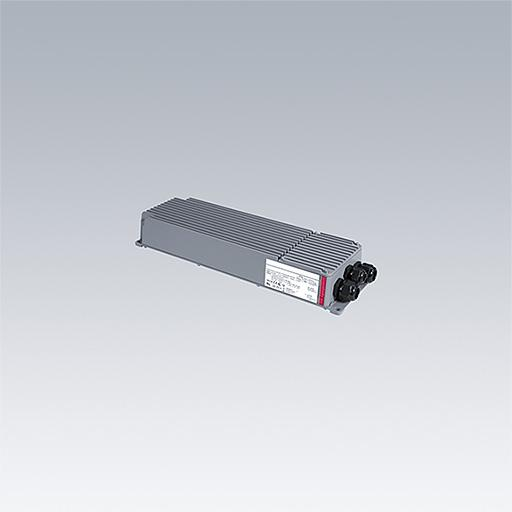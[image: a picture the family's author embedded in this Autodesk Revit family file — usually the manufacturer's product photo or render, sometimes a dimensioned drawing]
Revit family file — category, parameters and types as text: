
# Revit family: Thorn ALTIS GEN5 Gearbox-4 channel gearbox for RGBW
name_source: partatom
category: Electrical Fixtures
units: mm (PartAtom-declared; Revit-internal decimal feet)

## family parameters
Cut with Voids When Loaded = Yes
Host = Face
Maintain Annotation Orientation = No
Part Type = Normal
Room Calculation Point = Yes
Round Connector Dimension = Use Diameter
Shared = Yes

## types (1)
- ALG5 GB 1200W 0.85A 450V 4CH RGBW DMX/DA
    Apparent Load = 1200 VA
    Assembly Code = Pr_60_70_48_54
    Default Elevation = 0 mm  [stored 0 ft]
    Description = LED Control Gear
    Export Type to IFC As = IfcLightFixtureType
    Lamp = LED
    Luminaire Height = 77 mm  [stored 0.252625 ft]
    Luminaire Length = 500 mm  [stored 1.64042 ft]
    Luminaire Width = 152 mm  [stored 0.498688 ft]
    Manufacturer = Thorn Lighting
    Material Housing = Thorn-Aluminium-RAL 7043-Traffic Grey B
    Model = 96685716
    Power Factor = 1
    Type IFC Predefined Type = DIRECTIONSOURCE
    Type Image = TLG_ALG5_F_GB_LE_2100W.jpg
    URL = https://www.thornlighting.com
    Wattage = 1200 W

note: [stored X ft] marks values corroborated as IEEE doubles in the binary element streams (Revit-internal decimal feet)

## geometry (parser evidence)
native form markers: Sweep x2
no freeform markers — native parametric forms only
